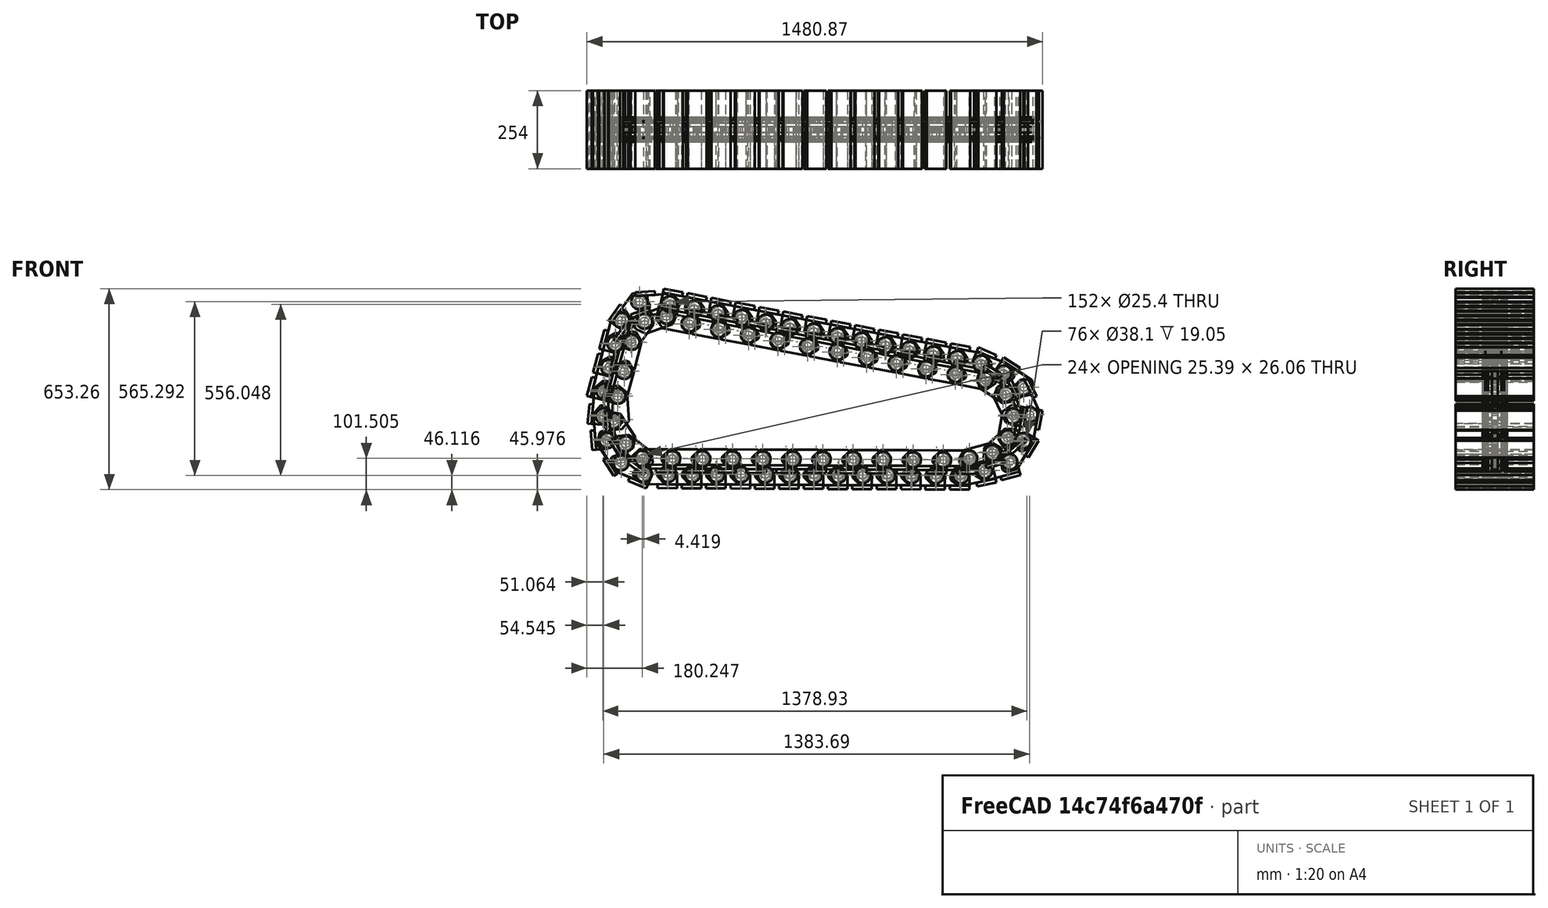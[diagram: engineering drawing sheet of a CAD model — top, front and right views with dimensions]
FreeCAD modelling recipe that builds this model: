
FCSTD DOCUMENT  (FreeCAD 0.16R6712 (Git))
Label: MT_track1
License: All rights reserved
LicenseURL: http://en.wikipedia.org/wiki/All_rights_reserved
objects: Sketcher::SketchObject×2, Part::FeaturePython×2, Part::Feature×1
note: 5 computed .brp shape members not serialized (recipe doc carries the construction recipe); baked Part::Feature solids carry a one-line shape summary decoded from their .brp

FEATURE [Sketcher::SketchObject] Sketch001  label="51in long"
  Placement = pos=(0,0,0) rot=(1,0,0;1.5708rad)
  sketch-geometry (14):
    g0: LineSegment StartX=-1058.51 StartY=-689.8 StartZ=0 EndX=-1002.49 EndY=-428.81 EndZ=0
    g1: LineSegment StartX=-1002.49 StartY=-428.81 StartZ=0 EndX=-965.847 EndY=-377.827 EndZ=0
    g2: LineSegment StartX=-965.847 StartY=-377.827 StartZ=0 EndX=-908.492 EndY=-363.488 EndZ=0
    g3: LineSegment StartX=-908.492 StartY=-363.488 StartZ=0 EndX=122.455 EndY=-564.351 EndZ=0
    g4: LineSegment StartX=122.455 StartY=-564.351 StartZ=0 EndX=207.428 EndY=-604.204 EndZ=0
    g5: LineSegment StartX=207.428 StartY=-604.204 StartZ=0 EndX=244.071 EndY=-690.237 EndZ=0
    g6: LineSegment StartX=244.071 StartY=-690.237 StartZ=0 EndX=231.326 EndY=-777.863 EndZ=0
    g7: LineSegment StartX=231.326 StartY=-777.863 StartZ=0 EndX=169.191 EndY=-841.591 EndZ=0
    g8: LineSegment StartX=169.191 StartY=-841.591 StartZ=0 EndX=73.5991 EndY=-855.93 EndZ=0
    g9: LineSegment StartX=73.5991 StartY=-855.93 StartZ=0 EndX=-920.187 EndY=-845.704 EndZ=0
    g10: LineSegment StartX=-920.187 StartY=-845.704 StartZ=0 EndX=-1007.27 EndY=-822.33 EndZ=0
    g11: LineSegment StartX=-1007.27 StartY=-822.33 StartZ=0 EndX=-1051.47 EndY=-762.477 EndZ=0
    g12: LineSegment StartX=-1051.47 StartY=-762.477 StartZ=0 EndX=-1058.51 EndY=-689.8 EndZ=0
    g13: LineSegment [constr] StartX=-1058.51 StartY=-690.237 StartZ=0 EndX=244.071 EndY=-690.237 EndZ=0
  constraints (16):
    c: Coincident(g0,g1)
    c: Coincident(g1,g2)
    c: Coincident(g2,g3)
    c: Coincident(g3,g4)
    c: Coincident(g4,g5)
    c: Coincident(g5,g6)
    c: Coincident(g6,g7)
    c: Coincident(g7,g8)
    c: Coincident(g8,g9)
    c: Coincident(g9,g10)
    c: Coincident(g10,g11)
    c: Coincident(g11,g12)
    c: Coincident(g12,g0)
    c: Horizontal(g13)
    c: Coincident(g5,g13)
    c: DistanceX(g13,g13) = 1302.58
FEATURE [Part::Feature] trackunitouterfused_001  label="trackunitouterfused_010"
  Placement = pos=(-282.278,53.991,-311.02) rot=(0,0,1;1.5708rad)
  shape: bbox 142.1 x 254 x 76.2 mm, 44 faces, 2 solids (baked)
FEATURE [Sketcher::SketchObject] Sketch  label="53.5in long"
  Placement = pos=(0,0,0) rot=(1,0,0;1.5708rad)
  sketch-geometry (21):
    g0: LineSegment StartX=-1081.99 StartY=-587.934 StartZ=0 EndX=-1038 EndY=-421.491 EndZ=0
    g1: LineSegment StartX=-1038 StartY=-421.491 StartZ=0 EndX=-998.77 EndY=-366.803 EndZ=0
    g2: LineSegment StartX=-998.77 StartY=-366.803 StartZ=0 EndX=-936.949 EndY=-344.214 EndZ=0
    g3: LineSegment StartX=-936.949 StartY=-344.214 StartZ=0 EndX=-877.505 EndY=-340.648 EndZ=0
    g4: LineSegment StartX=-877.505 StartY=-340.648 StartZ=0 EndX=127.096 EndY=-532.057 EndZ=0
    g5: LineSegment StartX=127.096 StartY=-532.057 StartZ=0 EndX=197.239 EndY=-561.779 EndZ=0
    g6: LineSegment StartX=197.239 StartY=-561.779 StartZ=0 EndX=235.284 EndY=-586.745 EndZ=0
    g7: LineSegment StartX=235.284 StartY=-586.745 StartZ=0 EndX=268.904 EndY=-657.727 EndZ=0
    g8: LineSegment StartX=268.904 StartY=-657.727 StartZ=0 EndX=276.754 EndY=-713.739 EndZ=0
    g9: LineSegment StartX=276.754 StartY=-713.739 StartZ=0 EndX=266.194 EndY=-772.21 EndZ=0
    g10: LineSegment StartX=266.194 StartY=-772.21 StartZ=0 EndX=237.661 EndY=-819.765 EndZ=0
    g11: LineSegment StartX=237.661 StartY=-819.765 StartZ=0 EndX=197.239 EndY=-856.62 EndZ=0
    g12: LineSegment StartX=197.239 StartY=-856.62 StartZ=0 EndX=131.851 EndY=-874.453 EndZ=0
    g13: LineSegment StartX=131.851 StartY=-874.453 StartZ=0 EndX=68.841 EndY=-887.531 EndZ=0
    g14: LineSegment StartX=68.841 StartY=-887.531 StartZ=0 EndX=-945.271 EndY=-882.775 EndZ=0
    g15: LineSegment StartX=-945.271 StartY=-882.775 StartZ=0 EndX=-1008.28 EndY=-856.62 EndZ=0
    g16: LineSegment StartX=-1008.28 StartY=-856.62 StartZ=0 EndX=-1038 EndY=-834.031 EndZ=0
    g17: LineSegment StartX=-1038 StartY=-834.031 StartZ=0 EndX=-1081.99 EndY=-766.265 EndZ=0
    g18: LineSegment StartX=-1081.99 StartY=-766.265 StartZ=0 EndX=-1089.12 EndY=-675.911 EndZ=0
    g19: LineSegment StartX=-1089.12 StartY=-675.911 StartZ=0 EndX=-1081.99 EndY=-587.934 EndZ=0
    g20: LineSegment [constr] StartX=-1089.04 StartY=-676.207 StartZ=0 EndX=271.494 EndY=-676.207 EndZ=0
  constraints (23):
    c: Coincident(g0,g1)
    c: Coincident(g1,g2)
    c: Coincident(g2,g3)
    c: Coincident(g3,g4)
    c: Coincident(g4,g5)
    c: Coincident(g5,g6)
    c: Coincident(g6,g7)
    c: Coincident(g7,g8)
    c: Coincident(g8,g9)
    c: Coincident(g9,g10)
    c: Coincident(g10,g11)
    c: Coincident(g11,g12)
    c: Coincident(g12,g13)
    c: Coincident(g13,g14)
    c: Coincident(g14,g15)
    c: Coincident(g15,g16)
    c: Coincident(g16,g17)
    c: Coincident(g17,g18)
    c: Coincident(g18,g19)
    c: Coincident(g19,g0)
    c: Horizontal(g20)
    c: PointOnObject(g20,g8)
    c: DistanceX(g20,g20) = 1360.54
FEATURE [Part::FeaturePython] PathArray  # WARN: FeaturePython — macro-defined, semantics opaque (R4)
  Align = true
  Base = -> trackunitouterfused_001
  Count = 34
  PathObj = -> Sketch
  Xlate = (0,0,0)
FEATURE [Part::FeaturePython] PathArray001  # WARN: FeaturePython — macro-defined, semantics opaque (R4)
  Align = true
  Base = -> trackunitouterfused_001
  Count = 42
  PathObj = -> Sketch
  Xlate = (0,0,-50.8)
